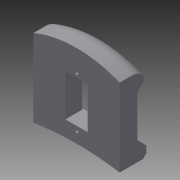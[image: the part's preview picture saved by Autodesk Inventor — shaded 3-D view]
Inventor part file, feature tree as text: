
AUTODESK INVENTOR PART (.ipt)
format: ipt  version: 2015 (Build 190159000, 159)  size: 206,848 bytes
history: native  units: mm
features: fillet x4, extrude x3, sketch x3, chamfer x2
ambient origin geometry x8: Origin, YZ Plane, XZ Plane, XY Plane, X Axis, Y Axis, Z Axis, Center Point
bodies: Solid1 (feature_tree)
feature tree (12):
  extrude  "Extrusion1"  Depth=23.2mm
  extrude  "Extrusion2"  Depth=15.0mm TaperAngle=0.0deg
  extrude  "Extrusion3"  Depth=0.2mm
  fillet  "Fillet1"  Radius=2.0mm
  chamfer  "Chamfer1"  Distance=2.35mm
  chamfer  "Chamfer2"  Distance=2.0mm
  fillet  "Fillet2"  Radius=5.0mm
  fillet  "Fillet3"  Radius=8.0mm
  fillet  "Fillet4"  Radius=5.0mm
  sketch  "Sketch1"  dims[d6=150.0mm d7=23.2mm]
  sketch  "Sketch2"  dims[d8=12.4mm d9=15.0mm d10=0.0mm]
  sketch  "Sketch3"  dims[d11=5.0mm d12=0.0mm d13=2.35mm d14=2.0mm d15=2.35mm d16=2.0mm d17=5.0mm d18=0.0mm d19=8.0mm d20=5.0mm d21=2.0mm d22=45.0deg d23=2.0mm d24=2.0mm d25=45.0deg d26=1.0mm d27=1.0mm d28=0.2mm]
